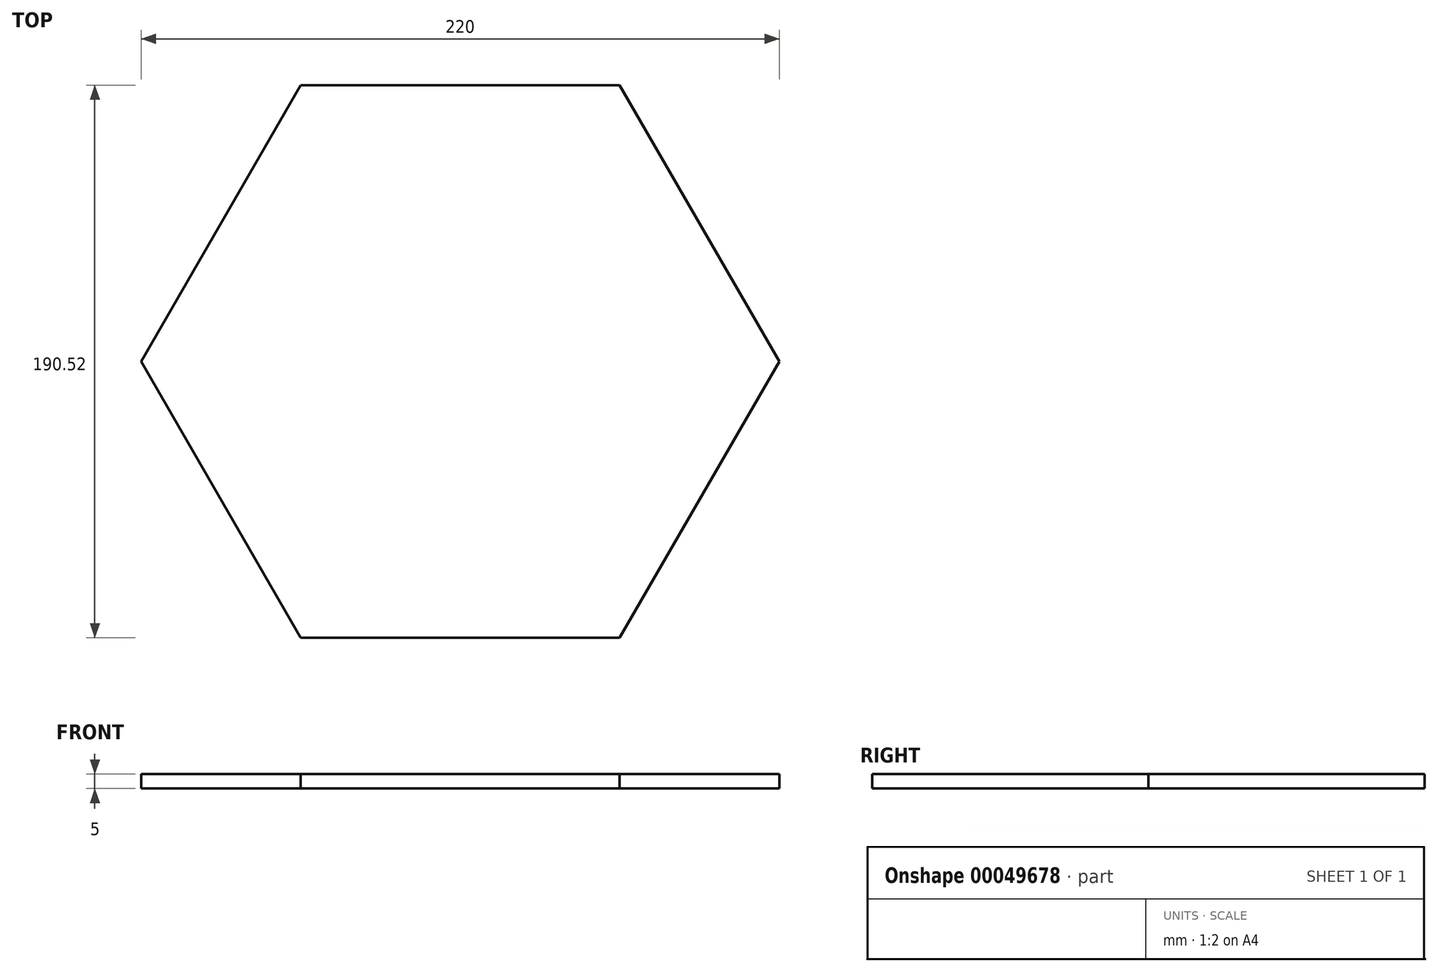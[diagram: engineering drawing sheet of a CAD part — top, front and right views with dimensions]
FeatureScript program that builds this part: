
annotation { "Feature Type Name" : "Feature", "Feature Type Description" : "" }
export const myFeature = defineFeature(function(context is Context, id is Id, definition is map)
    precondition{}
    {
        {
            var Q0;
            Q0=qCreatedBy(makeId("Top.planeOp"),FACE);
            var sketch = newSketch(context, id + "F0", { "sketchPlane" : qUnion([Q0])});
            skCircle(sketch, "E0.cCircle", {"center": v(0, 0) * mm, "radius": 95.26 * mm, "construction": true});
            skLineSegment(sketch, "E0.0", {"start": v(110, 0) * mm, "end": v(55, -95.26) * mm});
            skLineSegment(sketch, "E0.1", {"start": v(55, -95.26) * mm, "end": v(-55, -95.26) * mm});
            skLineSegment(sketch, "E0.2", {"start": v(-55, -95.26) * mm, "end": v(-110, 0) * mm});
            skLineSegment(sketch, "E0.3", {"start": v(-110, 0) * mm, "end": v(-55, 95.26) * mm});
            skLineSegment(sketch, "E0.4", {"start": v(-55, 95.26) * mm, "end": v(55, 95.26) * mm});
            skLineSegment(sketch, "E0.5", {"start": v(55, 95.26) * mm, "end": v(110, 0) * mm});
            skPoint(sketch, "E0.0.midPoint", {"position": v(82.5, -47.63) * mm});
            skLineSegment(sketch, "E1", {"start": v(0, 0) * mm, "end": v(110, 0) * mm, "construction": true});
            skSolve(sketch);
        }
        {
            var Q0;
            Q0=makeQuery(id+"F0.imprint","IMPRINT",FACE,{"disambiguationData":[TD([[makeQuery(id+"F0.imprint","IMPRINT",EDGE,{"derivedFrom":sQuery(id+"F0.wireOp",EDGE,"E0.0")}),-1.0]])]});
            extrude(context, id + "F1", {"entities" : qUnion([Q0]), "depth" : 5 * mm});
        }
    });
